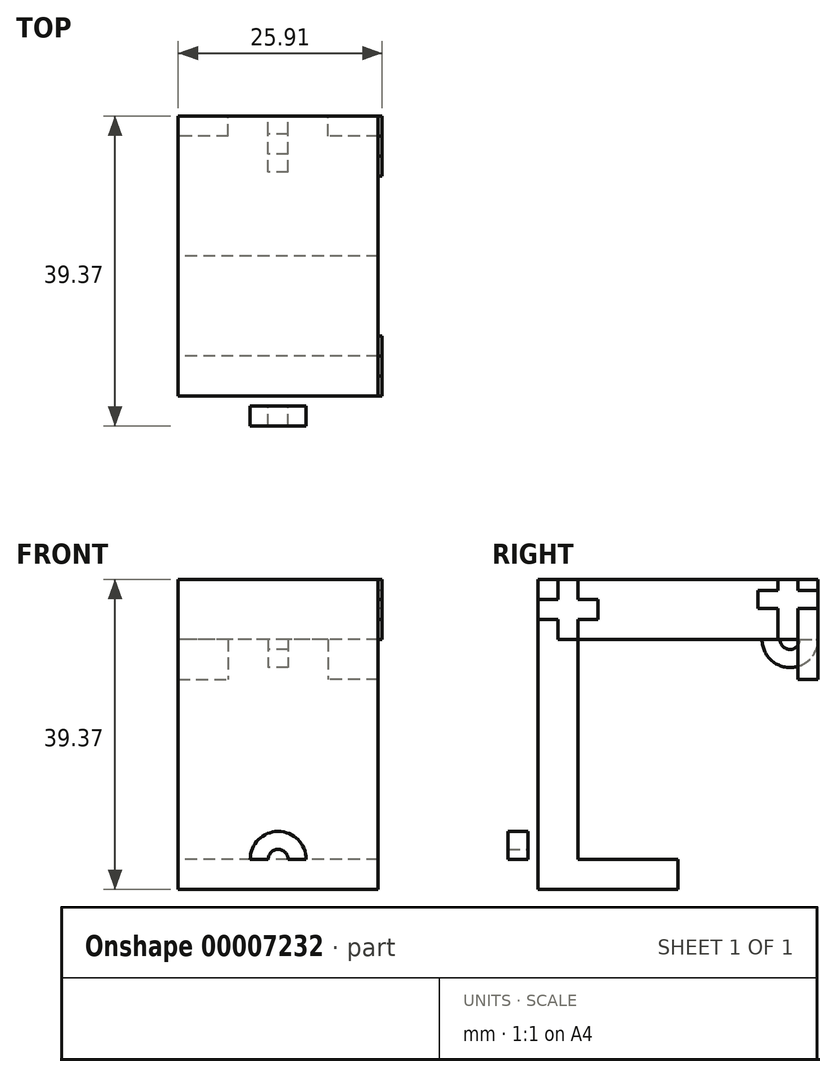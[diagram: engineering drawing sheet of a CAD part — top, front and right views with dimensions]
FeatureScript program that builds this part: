
annotation { "Feature Type Name" : "Feature", "Feature Type Description" : "" }
export const myFeature = defineFeature(function(context is Context, id is Id, definition is map)
    precondition{}
    {
        {
            var Q0;
            Q0=qCreatedBy(makeId("Right.planeOp"),FACE);
            var sketch = newSketch(context, id + "F0", { "sketchPlane" : qUnion([Q0])});
            skLineSegment(sketch, "E0", {"start": v(5.08, 31.75) * mm, "end": v(33.02, 31.75) * mm});
            skLineSegment(sketch, "E1", {"start": v(35.56, 31.75) * mm, "end": v(35.56, 39.37) * mm});
            skLineSegment(sketch, "E2", {"start": v(35.56, 39.37) * mm, "end": v(0, 39.37) * mm});
            skLineSegment(sketch, "E3", {"start": v(0, 39.37) * mm, "end": v(0, 3.8) * mm});
            skLineSegment(sketch, "E4", {"start": v(0, 0) * mm, "end": v(17.78, 0) * mm});
            skLineSegment(sketch, "E5", {"start": v(5.08, 31.75) * mm, "end": v(5.08, 3.81) * mm});
            skLineSegment(sketch, "E6", {"start": v(5.08, 3.8) * mm, "end": v(17.78, 3.8) * mm});
            skLineSegment(sketch, "E7", {"start": v(17.78, 3.8) * mm, "end": v(17.78, 0) * mm});
            skPoint(sketch, "E8", {"position": v(33.02, 31.75) * mm});
            skPoint(sketch, "E9", {"position": v(0, 31.75) * mm});
            skPoint(sketch, "E10", {"position": v(0, 3.8) * mm});
            skPoint(sketch, "E11.end.orphan", {"position": v(35.56, 24.13) * mm});
            skLineSegment(sketch, "E12", {"start": v(33.02, 31.75) * mm, "end": v(35.56, 31.75) * mm});
            skLineSegment(sketch, "E13", {"start": v(0, 0) * mm, "end": v(0, 3.8) * mm});
            skSolve(sketch);
        }
        {
            var Q0;
            Q0=qSketchRegion(id+"F0",true);
            extrude(context, id + "F1", {"entities" : qUnion([Q0]), "depth" : 25.4 * mm});
        }
        {
            var Q0;
            Q0=makeQuery(id+"F1.opExtrude","CAP_FACE",FACE,{"disambiguationData":[OSD([sQuery(id+"F0.wireOp",EDGE,"E0"),sQuery(id+"F0.wireOp",EDGE,"E1"),sQuery(id+"F0.wireOp",EDGE,"E2"),sQuery(id+"F0.wireOp",EDGE,"E3"),sQuery(id+"F0.wireOp",EDGE,"E4"),sQuery(id+"F0.wireOp",EDGE,"E5"),sQuery(id+"F0.wireOp",EDGE,"E6"),sQuery(id+"F0.wireOp",EDGE,"E7"),sQuery(id+"F0.wireOp",EDGE,"9346be45-5331-4f8b-a5d1-188d233d38a3"),sQuery(id+"F0.wireOp",EDGE,"c75531f2-f477-4a9c-aa0c-bcbe99bd43c6"),sQuery(id+"F0.wireOp",EDGE,"d47a0b08-9fc7-46c6-96c6-d1639268771b"),sQuery(id+"F0.wireOp",EDGE,"E12")])],"isStart":false});
            var sketch = newSketch(context, id + "F2", { "sketchPlane" : qUnion([Q0])});
            skArc(sketch, "E14", {"start": v(28.45, 31.75) * mm, "mid": v(32, 28.2) * mm, "end": v(35.56, 31.75) * mm});
            skArc(sketch, "E15", {"start": v(30.73, 31.75) * mm, "mid": v(32, 30.48) * mm, "end": v(33.27, 31.75) * mm});
            skLineSegment(sketch, "E16", {"start": v(30.73, 31.75) * mm, "end": v(28.45, 31.75) * mm});
            skLineSegment(sketch, "E17", {"start": v(28.45, 31.75) * mm, "end": v(30.73, 31.75) * mm});
            skLineSegment(sketch, "E18", {"start": v(33.27, 31.75) * mm, "end": v(35.56, 31.75) * mm});
            skSolve(sketch);
        }
        {
            var Q0;
            Q0=qSketchRegion(id+"F2",true);
            extrude(context, id + "F3", {"entities" : qUnion([Q0]), "depth" : 2.54 * mm});
        }
        {
            var Q0;
            Q0=makeQuery(id+"F3.opExtrude","SWEPT_BODY",BODY,{"disambiguationData":[OSD([sQuery(id+"F2.wireOp",EDGE,"E14"),sQuery(id+"F2.wireOp",EDGE,"E15"),sQuery(id+"F2.wireOp",EDGE,"E17"),sQuery(id+"F2.wireOp",EDGE,"E18")])]});
            var Q1;
            Q1=makeQuery(id+"F1.opExtrude","SWEPT_EDGE",EDGE,{"disambiguationData":[OSD([sQuery(id+"F0.wireOp",EDGE,"E1"),sQuery(id+"F0.wireOp",EDGE,"E12")])]});
            transform(context, id + "F4", {"entities" : qUnion([Q0]), "transformType" : TransformType.TRANSLATION_DISTANCE, "transformDirection" : qUnion([Q1]), "distance" : 13.97 * mm, "makeCopy" : false});
        }
        {
            var Q0;
            Q0=makeQuery(id+"F1.opExtrude","SWEPT_FACE",FACE,{"disambiguationData":[OSD([sQuery(id+"F0.wireOp",EDGE,"E7")])]});
            var sketch = newSketch(context, id + "F5", { "sketchPlane" : qUnion([Q0])});
            skArc(sketch, "E19", {"start": v(-9.14, 3.8) * mm, "mid": v(-12.7, 7.37) * mm, "end": v(-16.26, 3.8) * mm});
            skArc(sketch, "E20", {"start": v(-11.43, 3.8) * mm, "mid": v(-12.7, 5.08) * mm, "end": v(-13.97, 3.8) * mm});
            skLineSegment(sketch, "E21", {"start": v(-16.26, 3.8) * mm, "end": v(-13.97, 3.8) * mm});
            skLineSegment(sketch, "E22", {"start": v(-11.43, 3.8) * mm, "end": v(-9.14, 3.8) * mm});
            skSolve(sketch);
        }
        {
            var Q0;
            Q0=qSketchRegion(id+"F5",true);
            extrude(context, id + "F6", {"entities" : qUnion([Q0]), "oppositeDirection" : true, "depth" : 2.54 * mm});
        }
        {
            var Q0;
            Q0=makeQuery(id+"F6.opExtrude","SWEPT_BODY",BODY,{"disambiguationData":[OSD([sQuery(id+"F5.wireOp",EDGE,"E19"),sQuery(id+"F5.wireOp",EDGE,"E20"),sQuery(id+"F5.wireOp",EDGE,"E21"),sQuery(id+"F5.wireOp",EDGE,"E22")])]});
            var Q1;
            Q1=makeQuery(id+"F1.opExtrude","CAP_EDGE",EDGE,{"disambiguationData":[OSD([sQuery(id+"F0.wireOp",EDGE,"E6")])],"isStart":false});
            transform(context, id + "F7", {"entities" : qUnion([Q0]), "transformType" : TransformType.TRANSLATION_DISTANCE, "transformDirection" : qUnion([Q1]), "distance" : 19.05 * mm, "oppositeDirection" : true, "makeCopy" : false});
        }
        {
            var Q0;
            Q0=makeQuery(id+"F1.opExtrude","SWEPT_FACE",FACE,{"disambiguationData":[OSD([sQuery(id+"F0.wireOp",EDGE,"E1")])]});
            var sketch = newSketch(context, id + "F8", { "sketchPlane" : qUnion([Q0])});
            skLineSegment(sketch, "E23.bottom", {"start": v(-25.4, 31.75) * mm, "end": v(-19.05, 31.75) * mm});
            skLineSegment(sketch, "E23.top", {"start": v(-25.4, 26.67) * mm, "end": v(-19.05, 26.67) * mm});
            skLineSegment(sketch, "E23.left", {"start": v(-25.4, 31.75) * mm, "end": v(-25.4, 26.67) * mm});
            skLineSegment(sketch, "E23.right", {"start": v(-19.05, 31.75) * mm, "end": v(-19.05, 26.67) * mm});
            skLineSegment(sketch, "E24.bottom", {"start": v(0, 31.75) * mm, "end": v(-6.35, 31.75) * mm});
            skLineSegment(sketch, "E24.top", {"start": v(0, 26.67) * mm, "end": v(-6.35, 26.67) * mm});
            skLineSegment(sketch, "E24.left", {"start": v(0, 31.75) * mm, "end": v(0, 26.67) * mm});
            skLineSegment(sketch, "E24.right", {"start": v(-6.35, 31.75) * mm, "end": v(-6.35, 26.67) * mm});
            skLineSegment(sketch, "E25", {"start": v(-12.7, 31.75) * mm, "end": v(-12.7, 12.44) * mm, "construction": true});
            skSolve(sketch);
        }
        {
            var Q0;
            Q0=qSketchRegion(id+"F8",true);
            extrude(context, id + "F9", {"entities" : qUnion([Q0]), "oppositeDirection" : true, "depth" : 2.54 * mm});
        }
        {
            var Q0;
            Q0=makeQuery(id+"F1.opExtrude","SWEPT_BODY",BODY,{"disambiguationData":[OSD([sQuery(id+"F0.wireOp",EDGE,"E0"),sQuery(id+"F0.wireOp",EDGE,"E1"),sQuery(id+"F0.wireOp",EDGE,"E2"),sQuery(id+"F0.wireOp",EDGE,"E3"),sQuery(id+"F0.wireOp",EDGE,"E4"),sQuery(id+"F0.wireOp",EDGE,"E5"),sQuery(id+"F0.wireOp",EDGE,"E6"),sQuery(id+"F0.wireOp",EDGE,"E7"),sQuery(id+"F0.wireOp",EDGE,"9346be45-5331-4f8b-a5d1-188d233d38a3"),sQuery(id+"F0.wireOp",EDGE,"c75531f2-f477-4a9c-aa0c-bcbe99bd43c6"),sQuery(id+"F0.wireOp",EDGE,"d47a0b08-9fc7-46c6-96c6-d1639268771b"),sQuery(id+"F0.wireOp",EDGE,"E12")])]});
            var Q1;
            Q1=makeQuery(id+"F3.opExtrude","SWEPT_BODY",BODY,{"disambiguationData":[OSD([sQuery(id+"F2.wireOp",EDGE,"E14"),sQuery(id+"F2.wireOp",EDGE,"E15"),sQuery(id+"F2.wireOp",EDGE,"E17"),sQuery(id+"F2.wireOp",EDGE,"E18")])]});
            var Q2;
            Q2=makeQuery(id+"F9.opExtrude","SWEPT_BODY",BODY,{"disambiguationData":[OSD([sQuery(id+"F8.wireOp",EDGE,"E24.bottom"),sQuery(id+"F8.wireOp",EDGE,"E24.top"),sQuery(id+"F8.wireOp",EDGE,"E24.left"),sQuery(id+"F8.wireOp",EDGE,"E24.right")])]});
            var Q3;
            Q3=makeQuery(id+"F9.opExtrude","SWEPT_BODY",BODY,{"disambiguationData":[OSD([sQuery(id+"F8.wireOp",EDGE,"E23.bottom"),sQuery(id+"F8.wireOp",EDGE,"E23.top"),sQuery(id+"F8.wireOp",EDGE,"E23.left"),sQuery(id+"F8.wireOp",EDGE,"E23.right")])]});
            var Q4;
            Q4=makeQuery(id+"F6.opExtrude","SWEPT_BODY",BODY,{"disambiguationData":[OSD([sQuery(id+"F5.wireOp",EDGE,"E19"),sQuery(id+"F5.wireOp",EDGE,"E20"),sQuery(id+"F5.wireOp",EDGE,"E21"),sQuery(id+"F5.wireOp",EDGE,"E22")])]});
            booleanBodies(context, id + "F10", {"operationType" : BooleanOperationType.UNION, "tools" : qUnion([Q0, Q1, Q2, Q3, Q4])});
        }
        {
            var Q0;
            Q0=makeQuery(id+"F10.opBoolean","MERGE",FACE,{"derivedFrom":[makeQuery(id+"F1.opExtrude","CAP_FACE",FACE,{"disambiguationData":[OSD([sQuery(id+"F0.wireOp",EDGE,"E0"),sQuery(id+"F0.wireOp",EDGE,"E1"),sQuery(id+"F0.wireOp",EDGE,"E2"),sQuery(id+"F0.wireOp",EDGE,"E3"),sQuery(id+"F0.wireOp",EDGE,"E4"),sQuery(id+"F0.wireOp",EDGE,"E5"),sQuery(id+"F0.wireOp",EDGE,"E6"),sQuery(id+"F0.wireOp",EDGE,"E7"),sQuery(id+"F0.wireOp",EDGE,"9346be45-5331-4f8b-a5d1-188d233d38a3"),sQuery(id+"F0.wireOp",EDGE,"c75531f2-f477-4a9c-aa0c-bcbe99bd43c6"),sQuery(id+"F0.wireOp",EDGE,"d47a0b08-9fc7-46c6-96c6-d1639268771b"),sQuery(id+"F0.wireOp",EDGE,"E12")])],"isStart":false}),makeQuery(id+"F9.opExtrude","SWEPT_FACE",FACE,{"disambiguationData":[OSD([sQuery(id+"F8.wireOp",EDGE,"E23.left")])]})]});
            var sketch = newSketch(context, id + "F11", { "sketchPlane" : qUnion([Q0])});
            skLineSegment(sketch, "E26", {"start": v(17.78, 39.37) * mm, "end": v(17.78, 31.75) * mm, "construction": true});
            skLineSegment(sketch, "E27.bottom", {"start": v(0, 36.83) * mm, "end": v(2.54, 36.83) * mm});
            skLineSegment(sketch, "E27.top", {"start": v(0, 34.3) * mm, "end": v(2.54, 34.3) * mm});
            skLineSegment(sketch, "E27.left", {"start": v(0, 36.83) * mm, "end": v(0, 34.3) * mm});
            skLineSegment(sketch, "E27.right", {"start": v(7.62, 36.83) * mm, "end": v(7.62, 34.3) * mm});
            skLineSegment(sketch, "E28.bottom", {"start": v(27.94, 37.97) * mm, "end": v(30.48, 37.97) * mm});
            skLineSegment(sketch, "E28.top", {"start": v(27.94, 35.71) * mm, "end": v(30.48, 35.71) * mm});
            skLineSegment(sketch, "E28.left", {"start": v(27.94, 37.97) * mm, "end": v(27.94, 35.71) * mm});
            skLineSegment(sketch, "E28.right", {"start": v(35.56, 37.97) * mm, "end": v(35.56, 35.71) * mm});
            skLineSegment(sketch, "E29.bottom", {"start": v(2.54, 39.37) * mm, "end": v(5.08, 39.37) * mm});
            skLineSegment(sketch, "E29.top", {"start": v(2.54, 31.75) * mm, "end": v(5.08, 31.75) * mm});
            skLineSegment(sketch, "E29.left", {"start": v(2.54, 39.37) * mm, "end": v(2.54, 36.83) * mm});
            skLineSegment(sketch, "E29.right", {"start": v(5.08, 39.37) * mm, "end": v(5.08, 36.83) * mm});
            skLineSegment(sketch, "E30.bottom", {"start": v(30.48, 39.37) * mm, "end": v(33.02, 39.37) * mm});
            skLineSegment(sketch, "E30.top", {"start": v(30.48, 31.75) * mm, "end": v(33.02, 31.75) * mm});
            skLineSegment(sketch, "E30.left", {"start": v(30.48, 39.37) * mm, "end": v(30.48, 37.97) * mm});
            skLineSegment(sketch, "E30.right", {"start": v(33.02, 39.37) * mm, "end": v(33.02, 37.97) * mm});
            skPoint(sketch, "E31", {"position": v(2.54, 36.83) * mm});
            skPoint(sketch, "E32", {"position": v(5.08, 36.83) * mm});
            skPoint(sketch, "E33", {"position": v(5.08, 34.3) * mm});
            skPoint(sketch, "E34", {"position": v(2.54, 34.3) * mm});
            skPoint(sketch, "E35", {"position": v(30.48, 37.97) * mm});
            skPoint(sketch, "E36", {"position": v(33.02, 37.97) * mm});
            skPoint(sketch, "E37", {"position": v(33.02, 35.71) * mm});
            skPoint(sketch, "E38", {"position": v(30.48, 35.71) * mm});
            skLineSegment(sketch, "E39.trimOffspring", {"start": v(5.08, 34.3) * mm, "end": v(5.08, 31.75) * mm});
            skLineSegment(sketch, "E40.trimOffspring", {"start": v(5.08, 36.83) * mm, "end": v(7.62, 36.83) * mm});
            skLineSegment(sketch, "E41.trimOffspring", {"start": v(2.54, 34.3) * mm, "end": v(2.54, 31.75) * mm});
            skLineSegment(sketch, "E42.trimOffspring", {"start": v(5.08, 34.3) * mm, "end": v(7.62, 34.3) * mm});
            skLineSegment(sketch, "E43.trimOffspring", {"start": v(33.02, 37.97) * mm, "end": v(35.56, 37.97) * mm});
            skLineSegment(sketch, "E44.trimOffspring", {"start": v(30.48, 35.71) * mm, "end": v(30.48, 31.75) * mm});
            skLineSegment(sketch, "E45.trimOffspring", {"start": v(33.02, 35.71) * mm, "end": v(35.56, 35.71) * mm});
            skLineSegment(sketch, "E46.trimOffspring", {"start": v(33.02, 35.71) * mm, "end": v(33.02, 31.75) * mm});
            skSolve(sketch);
        }
        {
            var Q0;
            Q0=qSketchRegion(id+"F11",true);
            extrude(context, id + "F12", {"entities" : qUnion([Q0]), "depth" : 0.5 * mm});
        }
    });
